# Revit family: Hager-Orion_Plus-IP65-D300-Cl.II-Poly_double_encl-630A-Floor_installation-PT-pt
name_source: partatom
category: Electrical Equipment
units: mm (PartAtom-declared; Revit-internal decimal feet)

## family parameters
Cut with Voids When Loaded = No
Host = Face
Panel Configuration = Two Columns, Circuits Across
Part Type = Panelboard
Room Calculation Point = No
Round Connector Dimension = Use Diameter
Shared = No

## types (15) — shared parameters
EF000003 - Método de montagem = EV012274 - Instalação de piso
EF000007 - Cor = EV000270 - Cinzento
EF000049 - Profundidade = 300 mm  [stored 0.984252 ft]
EF000116 - Número RAL = 7035
EF001131 - Profundidade interior = 300 mm  [stored 0.984252 ft]
EF001596 - Material do corpo = EV000139 - Plástico
EF001613 - Integridade do circuito = EV000494 - Nenhum
EF005474 - Grau de proteção (IP) = EV006421 - IP65
EF006306 - Com fecho = Yes
EF007800 - Adequado para proteção contra raios = No
EF008873 - Corrente nominal (In) = 630 A
EF009170 - Espessura do material do invólucro = 2 mm  [stored 0.00656168 ft]
EF009171 - Espessura do material da porta/tampa = 2 mm  [stored 0.00656168 ft]
EF015940 - Tampa com libertação de sobrepressão = No
HG000003 - Gama = Orion Plus
HG000006 - Encastrado = No
HG000010 - Portas assimétricas = No
HG000023 - Recinto de secção dupla = Yes
HG000024 - Altura da secção inferior = 800 mm  [stored 2.62467 ft]
HG000026 - Instalação no chão = Yes
HG000027 - Altura da Plinta = 70 mm  [stored 0.229659 ft]
Manufacturer = Hager
Type Comments = Orion Plus
zero-valued in all types: Default Elevation, EF000218 - Profundidade incorporada, EF000437 - Número de entradas de condutores, EF009554 - Número de aberturas para placas de flange

## per-type parameters (varying)
| type | EF000008 - Largura | EF000040 - Altura | EF000118 - Com tampa de montagem | EF000266 - Número de linhas | EF000339 - Tipo de difusor | EF001088 - Extensão possível | EF002950 - Largura em número de módulos | EF003532 - Adequado para uso no exterior | EF004293 - Força de impacto | EF004427 - Número de módulos | EF004464 - Tipo de porta | EF006244 - Tampa/porta transparente | EF009212 - Tipo de tampa | HG000002 - Com porta ou tampa | HG000004 - Referência do Fabricante | HG000009 - Porta dupla |
| Instalação de piso IP65 L1100 A1150 P300  - FL360B | 1100 mm | 1150 mm | No | 3 | EV004216 - Porta | Yes | 0 | Yes | EV008784 - IK10 | 138 | EV002646 - Único | Yes | EV009916 - Com recuo | Yes | FL360B | Yes |
| Instalação de piso IP65 L1100 A1450 P300  - FL362B | 1100 mm | 1450 mm  [stored 4.75722 ft] | No | 3 | EV004216 - Porta | Yes | 0 | Yes | EV008784 - IK10 | 138 | EV002646 - Único | Yes | EV009916 - Com recuo | Yes | FL362B | Yes |
| Instalação de piso IP65 L1100 A1750 P300  - FL364B | 1100 mm | 1750 mm  [stored 5.74147 ft] | No | 3 | EV004216 - Porta | Yes | 0 | Yes | EV008784 - IK10 | 138 | EV002646 - Único | Yes | EV009916 - Com recuo | Yes | FL364B | Yes |
| Instalação de piso IP65 L1100 A1750 P300  - FL366B | 1100 mm | 1750 mm  [stored 5.74147 ft] | No | 5 | EV004216 - Porta | Yes | 0 | Yes | EV008784 - IK10 | 230 | EV002646 - Único | Yes | EV009916 - Com recuo | Yes | FL366B | Yes |
| Instalação de piso IP65 L1100 A2050 P300  - FL368B | 1100 mm | 2050 mm  [stored 6.72572 ft] | Yes | 5 | EV001012 - Tampa | No | 0 | No | EV006814 - IK08 | 230 | EV002646 - Único | No | EV000116 - Fechado | Yes | FL368B | Yes |
| Instalação de piso IP65 L600 A1150 P300  - FL340B | 600 mm | 1150 mm | No | 3 | EV004216 - Porta | Yes | 0 | Yes | EV008784 - IK10 | 69 | EV002646 - Único | Yes | EV009916 - Com recuo | Yes | FL340B | No |
| Instalação de piso IP65 L600 A1450 P300  - FL342B | 600 mm | 1450 mm  [stored 4.75722 ft] | No | 3 | EV004216 - Porta | Yes | 0 | Yes | EV008784 - IK10 | 69 | EV002646 - Único | Yes | EV009916 - Com recuo | No | FL342B | No |
| Instalação de piso IP65 L600 A1750 P300  - FL344B | 600 mm | 1750 mm  [stored 5.74147 ft] | No | 9 | EV004216 - Porta | Yes | 23 | No |  | 0 |  | Yes | EV009916 - Com recuo | Yes | FL344B | No |
| Instalação de piso IP65 L600 A1750 P300  - FL346B | 600 mm | 1750 mm  [stored 5.74147 ft] | No | 5 | EV004216 - Porta | Yes | 0 | Yes | EV008784 - IK10 | 115 | EV002646 - Único | Yes | EV009916 - Com recuo | Yes | FL346B | No |
| Instalação de piso IP65 L600 A2050 P300  - FL348B | 600 mm | 2050 mm  [stored 6.72572 ft] | No | 3 | EV004216 - Porta | Yes | 0 | Yes | EV008784 - IK10 | 115 | EV002646 - Único | Yes | EV009916 - Com recuo | Yes | FL348B | No |
| Instalação de piso IP65 L850 A1150 P300  - FL350B | 850 mm  [stored 2.78871 ft] | 1150 mm | No | 3 | EV004216 - Porta | Yes | 0 | Yes | EV008784 - IK10 | 111 | EV002646 - Único | Yes | EV009916 - Com recuo | Yes | FL350B | No |
| Instalação de piso IP65 L850 A1450 P300  - FL352B | 850 mm  [stored 2.78871 ft] | 1450 mm  [stored 4.75722 ft] | Yes | 3 | EV001012 - Tampa | No | 0 | No | EV006814 - IK08 | 111 | EV002646 - Único | No | EV000116 - Fechado | Yes | FL352B | No |
| Instalação de piso IP65 L850 A1750 P300  - FL354B | 850 mm  [stored 2.78871 ft] | 1750 mm  [stored 5.74147 ft] | Yes | 3 | EV001012 - Tampa | No | 0 | No | EV006814 - IK08 | 111 | EV002646 - Único | No | EV000116 - Fechado | Yes | FL354B | No |
| Instalação de piso IP65 L850 A1750 P300  - FL356B | 850 mm  [stored 2.78871 ft] | 1750 mm  [stored 5.74147 ft] | No | 5 | EV004216 - Porta | Yes | 0 | Yes | EV008784 - IK10 | 185 | EV002646 - Único | Yes | EV009916 - Com recuo | Yes | FL356B | No |
| Instalação de piso IP65 L850 A2050 P300  - FL358B | 850 mm  [stored 2.78871 ft] | 2050 mm  [stored 6.72572 ft] | No | 5 | EV004216 - Porta | Yes | 0 | Yes | EV008784 - IK10 | 185 | EV002646 - Único | Yes | EV009916 - Com recuo | Yes | FL358B | No |

note: [stored X ft] marks values corroborated as IEEE doubles in the binary element streams (Revit-internal decimal feet)

## geometry (parser evidence)
native form markers: Sweep x10
no freeform markers — native parametric forms only
